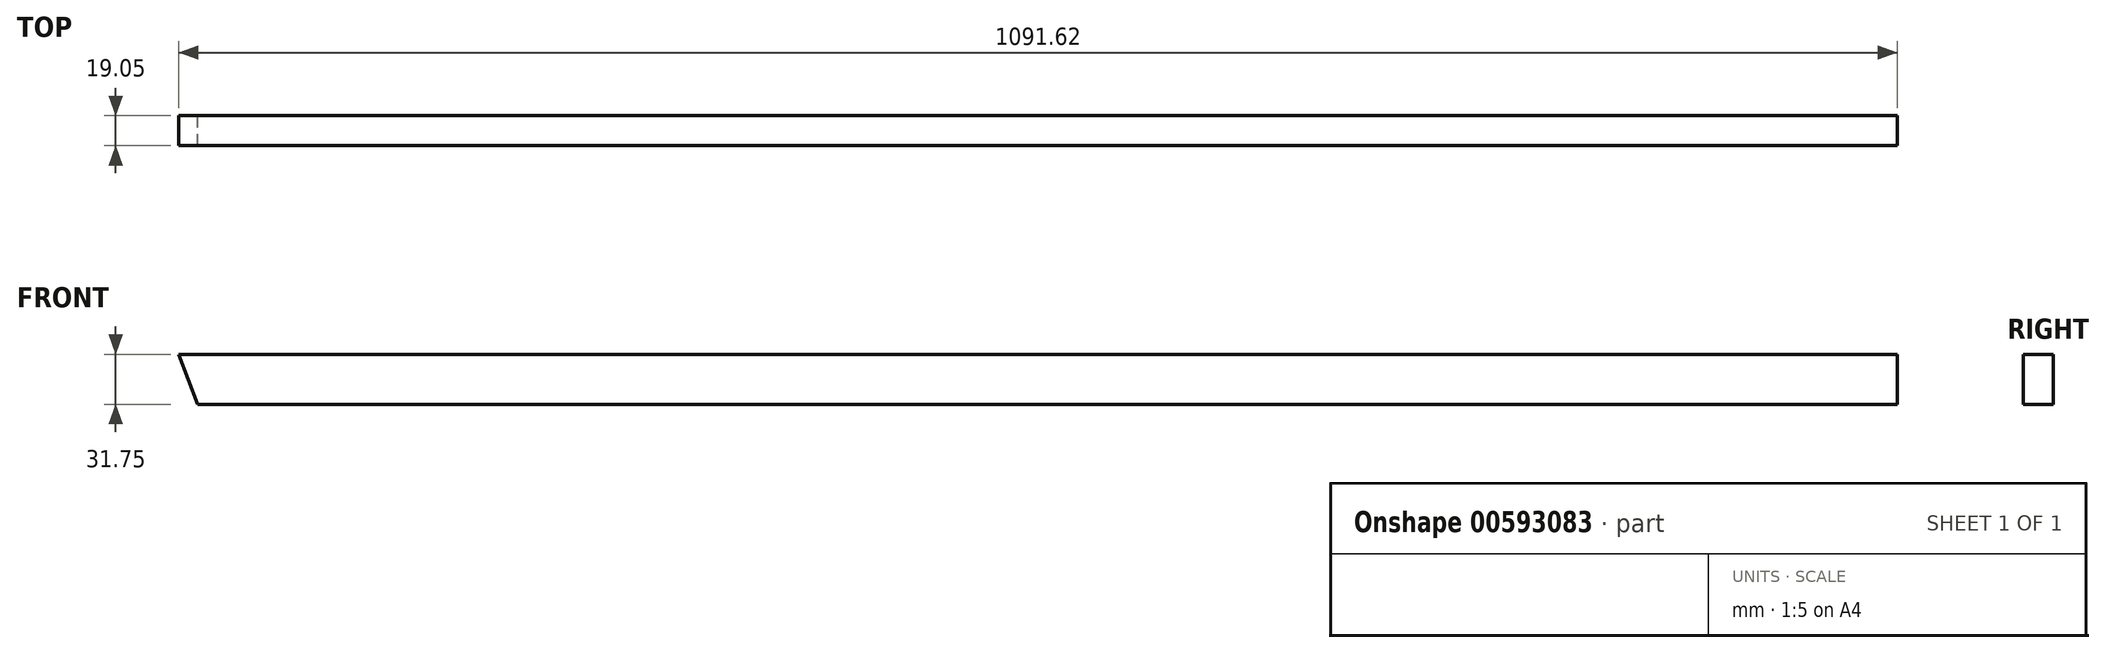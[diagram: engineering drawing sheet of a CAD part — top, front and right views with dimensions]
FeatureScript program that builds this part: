
annotation { "Feature Type Name" : "Feature", "Feature Type Description" : "" }
export const myFeature = defineFeature(function(context is Context, id is Id, definition is map)
    precondition{}
    {
        {
            var Q0;
            Q0=qCreatedBy(makeId("Front.planeOp"),FACE);
            var sketch = newSketch(context, id + "F0", { "sketchPlane" : qUnion([Q0])});
            skLineSegment(sketch, "E0", {"start": v(0, 0) * mm, "end": v(-1079.5, 0) * mm});
            skLineSegment(sketch, "E1", {"start": v(-1079.5, 0) * mm, "end": v(-1091.62, 31.75) * mm});
            skLineSegment(sketch, "E2", {"start": v(0, 0) * mm, "end": v(0, 31.75) * mm});
            skLineSegment(sketch, "E3", {"start": v(0, 31.75) * mm, "end": v(-1091.51, 31.75) * mm});
            skLineSegment(sketch, "E4", {"start": v(-1091.51, 31.75) * mm, "end": v(-1091.62, 31.75) * mm});
            skPoint(sketch, "E5.orphan", {"position": v(-1190.96, 291.96) * mm});
            skSolve(sketch);
        }
        {
            var Q0;
            Q0=makeQuery(id+"F0.imprint","IMPRINT",FACE,{"disambiguationData":[TD([[makeQuery(id+"F0.imprint","IMPRINT",EDGE,{"derivedFrom":sQuery(id+"F0.wireOp",EDGE,"E0")}),-1.0]])]});
            var Q1;
            Q1=sQuery(id+"F0.wireOp",EDGE,"E3");
            var Q2;
            Q2=sQuery(id+"F0.wireOp",EDGE,"E0");
            extrude(context, id + "F1", {"entities" : qUnion([Q0]), "surfaceEntities" : qUnion([Q1, Q2]), "depth" : 19.05 * mm, "offsetDistance" : 25.4 * mm});
        }
    });
